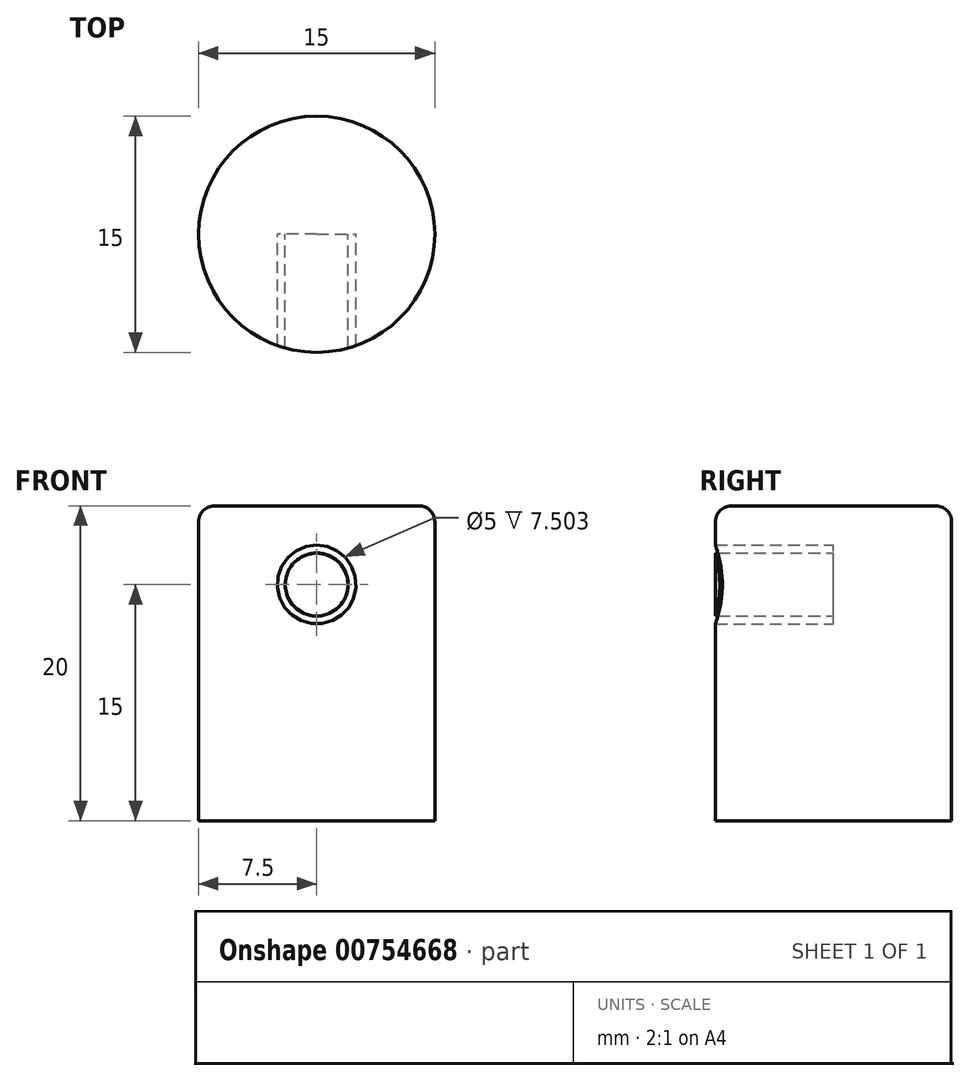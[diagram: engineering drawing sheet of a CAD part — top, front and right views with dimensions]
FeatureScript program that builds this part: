
annotation { "Feature Type Name" : "Feature", "Feature Type Description" : "" }
export const myFeature = defineFeature(function(context is Context, id is Id, definition is map)
    precondition{}
    {
        {
            var Q0;
            Q0=qCreatedBy(makeId("Top.planeOp"),FACE);
            var sketch = newSketch(context, id + "F0", { "sketchPlane" : qUnion([Q0])});
            skCircle(sketch, "E0", {"center": v(0, 0) * mm, "radius": 12.5 * mm});
            skSolve(sketch);
        }
        {
            var Q0;
            Q0=makeQuery(id+"F0.imprint","IMPRINT",FACE,{"disambiguationData":[TD([[makeQuery(id+"F0.imprint","IMPRINT",EDGE,{"derivedFrom":sQuery(id+"F0.wireOp",EDGE,"E0")}),1.0]])]});
            extrude(context, id + "F1", {"entities" : qUnion([Q0]), "depth" : 20 * mm, "offsetDistance" : 25 * mm});
        }
        {
            var Q0;
            Q0=makeQuery(id+"F1.opExtrude","CAP_FACE",FACE,{"disambiguationData":[OSD([sQuery(id+"F0.wireOp",EDGE,"E0")])],"isStart":false});
            var sketch = newSketch(context, id + "F2", { "sketchPlane" : qUnion([Q0])});
            skCircle(sketch, "E1", {"center": v(0, 0) * mm, "radius": 9 * mm});
            skSolve(sketch);
        }
        {
            var Q0;
            Q0=makeQuery(id+"F2.imprint","IMPRINT",FACE,{"disambiguationData":[TD([[makeQuery(id+"F2.imprint","IMPRINT",EDGE,{"derivedFrom":sQuery(id+"F2.wireOp",EDGE,"E1")}),1.0]])]});
            extrude(context, id + "F3", {"entities" : qUnion([Q0]), "operationType" : NewBodyOperationType.ADD, "depth" : 10 * mm, "offsetDistance" : 25 * mm});
        }
        {
            var Q0;
            Q0=makeQuery(id+"F3.opExtrude","CAP_FACE",FACE,{"disambiguationData":[OSD([sQuery(id+"F2.wireOp",EDGE,"E1")])],"isStart":false});
            var sketch = newSketch(context, id + "F4", { "sketchPlane" : qUnion([Q0])});
            skCircle(sketch, "E2", {"center": v(0, 0) * mm, "radius": 7.5 * mm});
            skSolve(sketch);
        }
        {
            var Q0;
            Q0=makeQuery(id+"F4.imprint","IMPRINT",FACE,{"disambiguationData":[TD([[makeQuery(id+"F4.imprint","IMPRINT",EDGE,{"derivedFrom":sQuery(id+"F4.wireOp",EDGE,"E2")}),1.0]])]});
            extrude(context, id + "F5", {"entities" : qUnion([Q0]), "operationType" : NewBodyOperationType.ADD, "depth" : 20 * mm, "offsetDistance" : 25 * mm});
        }
        {
            var Q0;
            Q0=makeQuery(id+"F1.opExtrude","CAP_EDGE",EDGE,{"disambiguationData":[OSD([sQuery(id+"F0.wireOp",EDGE,"E0")])],"isStart":false});
            fillet(context, id + "F6", {"entities" : qUnion([Q0]), "radius" : 2 * mm, "tangentPropagation" : true, "allowEdgeOverflow" : false});
        }
        {
            var Q0;
            Q0=makeQuery(id+"F3.opExtrude","CAP_EDGE",EDGE,{"disambiguationData":[OSD([sQuery(id+"F2.wireOp",EDGE,"E1")])],"isStart":false});
            chamfer(context, id + "F7", {"entities" : qUnion([Q0]), "width" : 1 * mm, "tangentPropagation" : true});
        }
        {
            var Q0;
            Q0=makeQuery(id+"F5.opExtrude","CAP_EDGE",EDGE,{"disambiguationData":[OSD([sQuery(id+"F4.wireOp",EDGE,"E2")])],"isStart":false});
            fillet(context, id + "F8", {"entities" : qUnion([Q0]), "radius" : 1 * mm, "tangentPropagation" : true, "allowEdgeOverflow" : false});
        }
        {
            var Q0;
            Q0=qCreatedBy(makeId("Front.planeOp"),FACE);
            var sketch = newSketch(context, id + "F9", { "sketchPlane" : qUnion([Q0])});
            skCircle(sketch, "E3", {"center": v(0, 45) * mm, "radius": 2.5 * mm});
            skCircle(sketch, "E4", {"center": v(0, 45) * mm, "radius": 2 * mm});
            skSolve(sketch);
        }
        {
            var Q0;
            Q0=qSketchRegion(id+"F9",true);
            extrude(context, id + "F10", {"entities" : qUnion([Q0]), "operationType" : NewBodyOperationType.REMOVE, "depth" : 25 * mm, "offsetDistance" : 25 * mm});
        }
        {
            var Q0;
            Q0=makeQuery(id+"F1.opExtrude","CAP_FACE",FACE,{"disambiguationData":[OSD([sQuery(id+"F0.wireOp",EDGE,"E0")])],"isStart":true});
            var sketch = newSketch(context, id + "F11", { "sketchPlane" : qUnion([Q0])});
            skCircle(sketch, "E5", {"center": v(0, 0) * mm, "radius": 3.5 * mm});
            skCircle(sketch, "E6", {"center": v(0, 0) * mm, "radius": 2.5 * mm});
            skSolve(sketch);
        }
        {
            var Q0;
            Q0=makeQuery(id+"F11.imprint","IMPRINT",FACE,{"disambiguationData":[TD([[makeQuery(id+"F11.imprint","IMPRINT",EDGE,{"derivedFrom":sQuery(id+"F11.wireOp",EDGE,"E5")}),1.0]])]});
            extrude(context, id + "F12", {"entities" : qUnion([Q0]), "operationType" : NewBodyOperationType.ADD, "depth" : 50 * mm, "offsetDistance" : 25 * mm});
        }
        {
            var Q0;
            Q0=makeQuery(id+"F12.opExtrude","CAP_FACE",FACE,{"disambiguationData":[OSD([sQuery(id+"F11.wireOp",EDGE,"E5"),sQuery(id+"F11.wireOp",EDGE,"E6")])],"isStart":false});
            var sketch = newSketch(context, id + "F13", { "sketchPlane" : qUnion([Q0])});
            skCircle(sketch, "E7", {"center": v(0, 0) * mm, "radius": 34.81 * mm});
            skSolve(sketch);
        }
        {
            var Q0;
            Q0=makeQuery(id+"F13.imprint","IMPRINT",FACE,{"disambiguationData":[TD([[makeQuery(id+"F13.imprint","IMPRINT",EDGE,{"derivedFrom":sQuery(id+"F13.wireOp",EDGE,"E7")}),1.0]])]});
            var Q1;
            Q1=makeQuery(id+"F13.imprint","IMPRINT",FACE,{"disambiguationData":[TD([[makeQuery(id+"F13.imprint","IMPRINT",EDGE,{"derivedFrom":makeQuery(id+"F12.opExtrude","CAP_EDGE",EDGE,{"disambiguationData":[OSD([sQuery(id+"F11.wireOp",EDGE,"E6")])],"isStart":false})}),1.0]])]});
            var Q2;
            Q2=makeQuery(id+"F13.imprint","IMPRINT",FACE,{"disambiguationData":[TD([[makeQuery(id+"F13.imprint","IMPRINT",EDGE,{"derivedFrom":makeQuery(id+"F12.opExtrude","CAP_EDGE",EDGE,{"disambiguationData":[OSD([sQuery(id+"F11.wireOp",EDGE,"E5")])],"isStart":false})}),1.0]])]});
            var Q3;
            Q3=makeQuery(id+"F3.opExtrude","CAP_FACE",FACE,{"disambiguationData":[OSD([sQuery(id+"F2.wireOp",EDGE,"E1")])],"isStart":false});
            extrude(context, id + "F14", {"entities" : qUnion([Q0, Q1, Q2]), "operationType" : NewBodyOperationType.REMOVE, "endBound" : BoundingType.UP_TO_SURFACE, "oppositeDirection" : true, "depth" : 25 * mm, "endBoundEntityFace" : qUnion([Q3]), "offsetDistance" : 25 * mm});
        }
    });
